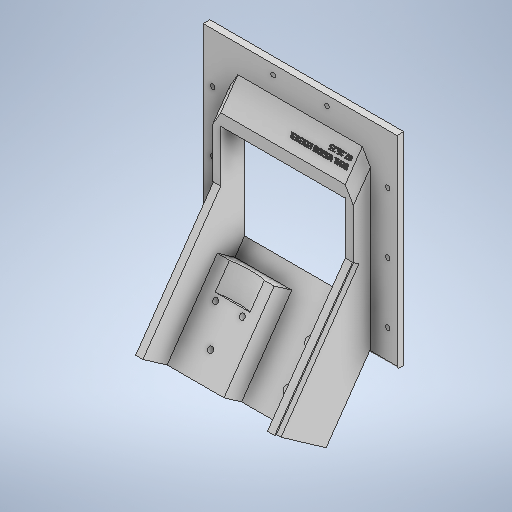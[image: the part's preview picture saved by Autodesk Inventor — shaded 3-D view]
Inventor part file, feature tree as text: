
AUTODESK INVENTOR PART (.ipt)
format: ipt  version: 2025.2 (Build 292293000, 293)  size: 1,263,104 bytes
history: native  units: in
note: dims shown in document units (in); Inventor stores cm internally (conversion verified against a paired STEP export)
features: sketch x35, extrude x30, plane x5, projected_geometry x3, move_body x1, chamfer x1, fillet x1, hole x1
ambient origin geometry x8: Origin, YZ Plane, XZ Plane, XY Plane, X Axis, Y Axis, Z Axis, Center Point
bodies: Solid1 (feature_tree)
feature tree (77):
  extrude  "Extrusion1"  Depth=0.1969in TaperAngle=0.0deg
  move_body  "Move Body1"
  plane  "Work Plane1"
  sketch  "Sketch5"  dims[d5=1.7717in d6=1.7717in d7=1.7717in d8=1.7717in d9=0.8108in d10=90.0deg d11=0.0787in d12=0.3701in d13=0.4252in d14=0.1362in d15=-0.0984in d16=-0.0591in d17=0.0in]
  plane  "Work Plane2"
  extrude  "Extrusion4"  TaperAngle=0.0deg  [1 undecoded]
  extrude  "Extrusion6"  Depth=0.2405in
  extrude  "Extrusion8"  Depth=2.5591in TaperAngle=0.0deg
  chamfer  "Chamfer1"  [1 undecoded]
  extrude  "Extrusion11"  Depth=0.2362in
  plane  "Work Plane3"
  extrude  "Extrusion13"  Depth=0.1969in TaperAngle=0.0deg
  plane  "Work Plane4"
  plane  "Work Plane6"
  extrude  "Extrusion21"  Depth=0.5027in
  extrude  "Extrusion22"  Depth=0.5027in
  extrude  "Extrusion25"  Depth=1.1811in TaperAngle=0.0deg
  extrude  "Extrusion26"  Depth=0.1969in
  sketch  "Sketch33"  dims[d100=3.6403in d101=2.7717in]
  extrude  "Extrusion27"  Depth=0.2362in TaperAngle=0.0deg
  extrude  "Extrusion28"  Depth=3.6403in
  sketch  "Sketch36"  dims[d124=0.9712in d125=0.0in d126=0.5906in d127=0.0in]
  extrude  "Extrusion29"  Depth=0.6299in TaperAngle=0.0deg
  extrude  "Extrusion30"  Depth=0.1575in
  extrude  "Extrusion31"  Depth=0.5906in TaperAngle=0.0deg
  sketch  "Sketch39"  dims[d139=0.1181in d140=0.0in d141=0.6299in]
  extrude  "Extrusion32"  Depth=11.3469in TaperAngle=0.0deg
  fillet  "Fillet1"  Radius=0.4331in
  extrude  "Extrusion33"  Depth=0.4331in
  extrude  "Extrusion34"  Depth=0.1181in
  extrude  "Extrusion35"  Depth=0.2756in
  sketch  "Sketch45"  dims[d164=0.1181in d165=0.0in d168=0.5906in d169=0.0in]
  extrude  "Extrusion37"  TaperAngle=0.0deg  [1 undecoded]
  extrude  "Extrusion38"  Depth=0.1181in TaperAngle=0.0deg
  extrude  "Extrusion40"  Depth=0.1181in TaperAngle=0.0deg
  extrude  "Extrusion41"  Depth=0.1181in TaperAngle=0.0deg
  extrude  "Extrusion43"  TaperAngle=0.0deg  [1 undecoded]
  extrude  "Extrusion44"  TaperAngle=0.0deg  [1 undecoded]
  extrude  "Extrusion46"  TaperAngle=0.0deg  [1 undecoded]
  extrude  "Extrusion47"  Depth=0.5906in
  extrude  "Extrusion48"  Depth=0.0394in TaperAngle=0.0deg
  sketch  "Sketch61"  dims[d251=0.1969in]
  extrude  "Extrusion50"  Depth=3.9671in TaperAngle=0.0deg
  extrude  "Extrusion51"  Depth=0.1969in
  sketch  "Sketch1"  dims[d1=0.5512in d2=0.1969in d3=0.0in]
  sketch  "Sketch6"  dims[d18=0.2749in d24=0.2405in]
  sketch  "Sketch8"  dims[d25=2.7559in d26=0.0in d29=2.5591in d30=0.0in d36=0.0in d37=0.0in]
  sketch  "Sketch12"  dims[d42=0.2362in d43=0.2362in]
  sketch  "Sketch15"  dims[d52=0.2362in d53=0.0787in d54=45.0deg d55=0.1969in d56=0.0in]
  sketch  "Sketch17"  dims[d59=0.5906in d60=0.0in d76=0.5027in]
  sketch  "Sketch27"  dims[d77=0.5027in d78=0.5027in]
  sketch  "Sketch28"  dims[d79=0.5027in d81=1.1811in d82=0.0in]
  sketch  "Sketch31"  dims[d83=0.0in d84=0.0in d91=0.1969in]
  sketch  "Sketch32"  dims[d94=0.2362in d95=0.0in d96=0.2362in d97=0.0in]
  sketch  "Sketch34"  dims[d112=1.9685in d113=0.6299in d114=0.0in]
  sketch  "Sketch35"  dims[d115=0.1575in d117=0.1575in d121=1.9685in d122=0.7874in d123=0.9331in]
  sketch  "Sketch37"  dims[d128=11.3469in d129=0.0in d130=11.3469in d131=0.0in d136=0.4331in]
  sketch  "Sketch38"  dims[d137=0.4331in d138=0.4331in]
  sketch  "Sketch40"  dims[d142=0.0787in d147=0.2756in]
  sketch  "Sketch41"  dims[d149=0.2756in d150=0.0in d151=0.0in]
  sketch  "Sketch42"  dims[d154=0.1181in d155=0.0in d156=0.1181in d157=0.0in]
  sketch  "Sketch44"  dims[d158=0.5906in d160=0.1181in d161=0.0in d162=0.1969in d163=0.0in]
  projected_geometry  "Projected Loop2"
  projected_geometry  "Projected Loop3"
  projected_geometry  "Projected Loop5"
  sketch  "Sketch47"  dims[d170=4.7244in d171=0.0in d174=0.0in d175=0.0in]
  sketch  "Sketch49"  dims[d176=0.7313in d177=0.0in d186=0.0in d187=0.0in]
  sketch  "Sketch50"  dims[d188=0.0in d189=0.0in d194=0.0in d195=0.0in]
  sketch  "Sketch52"  dims[d196=1.1024in d197=0.5906in]
  sketch  "Sketch53"  dims[d198=0.0394in d199=0.0in d200=0.0394in d201=0.0in]
  sketch  "Sketch56"  dims[d235=6.1063in d236=0.0in d244=3.9671in d245=0.0in]
  sketch  "Sketch58"  dims[d246=0.9963in d248=0.1969in]
  sketch  "Sketch59"  dims[d249=0.1378in d250=60.0deg]
  sketch  "Sketch63"  dims[d252=0.1378in]
  sketch  "Sketch64"  dims[d253=60.0deg d38=0.0197in d39=0.0344in d57=0.0197in d58=0.0344in d159=0.0344in d178=0.0in d179=0.0in d180=0.0in d181=0.0in d202=0.0197in d203=0.0344in]
  sketch  "Sketch2"  dims[d4=0.315in]
  hole  "Hole1"  [1 undecoded]
note: 7 required parameter values undecoded (feature->parameter linkage not recoverable at this tier; creation-order binding heuristic only, values carry confidence <= 0.55)
